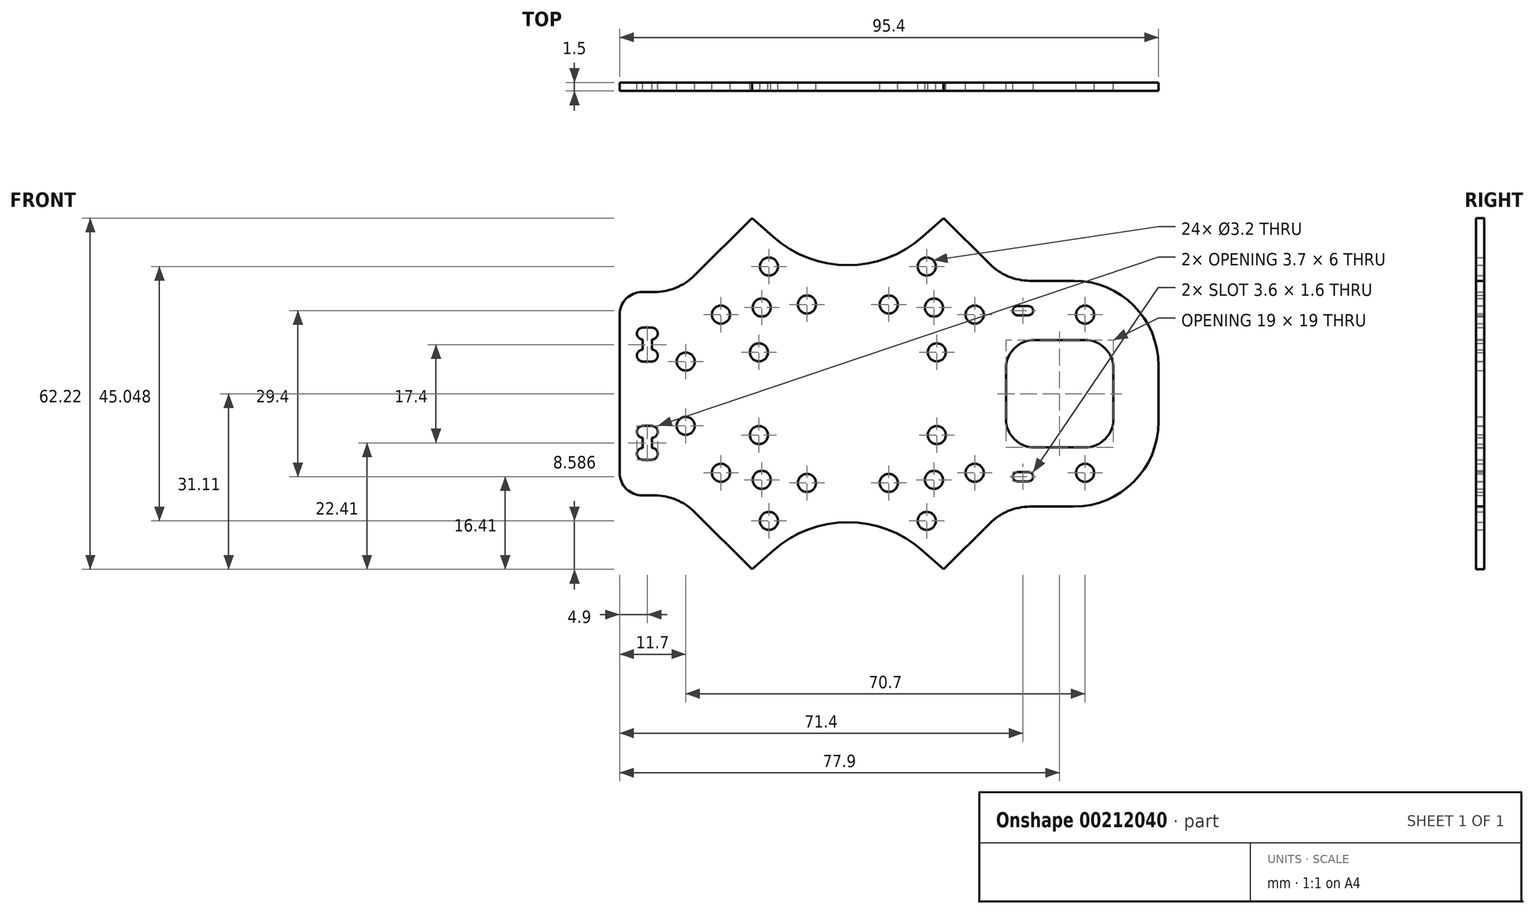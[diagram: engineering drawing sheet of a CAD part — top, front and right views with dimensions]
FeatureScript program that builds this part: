
annotation { "Feature Type Name" : "Feature", "Feature Type Description" : "" }
export const myFeature = defineFeature(function(context is Context, id is Id, definition is map)
    precondition{}
    {
        {
            var Q0;
            Q0=qCreatedBy(makeId("Front.planeOp"),FACE);
            var sketch = newSketch(context, id + "F0", { "sketchPlane" : qUnion([Q0])});
            skPoint(sketch, "E0", {"position": v(0, 0) * mm});
            skCircle(sketch, "E1", {"center": v(15.73, 7.32) * mm, "radius": 1.6 * mm});
            skCircle(sketch, "E2", {"center": v(13.97, 22.52) * mm, "radius": 1.6 * mm});
            skCircle(sketch, "E3", {"center": v(7.25, 15.8) * mm, "radius": 1.6 * mm});
            skCircle(sketch, "E4", {"center": v(22.45, 14) * mm, "radius": 1.6 * mm});
            skCircle(sketch, "E5", {"center": v(15.25, 15.25) * mm, "radius": 1.6 * mm});
            skCircle(sketch, "E6.MirrorC", {"center": v(-15.73, 7.32) * mm, "radius": 1.6 * mm});
            skCircle(sketch, "E7.MirrorC", {"center": v(-13.97, 22.52) * mm, "radius": 1.6 * mm});
            skCircle(sketch, "E8.MirrorC", {"center": v(-7.25, 15.8) * mm, "radius": 1.6 * mm});
            skCircle(sketch, "E9.MirrorC", {"center": v(-22.45, 14) * mm, "radius": 1.6 * mm});
            skCircle(sketch, "E10.MirrorC", {"center": v(-15.25, 15.25) * mm, "radius": 1.6 * mm});
            skCircle(sketch, "E11.MirrorC", {"center": v(-15.25, -15.25) * mm, "radius": 1.6 * mm});
            skCircle(sketch, "E12.MirrorC", {"center": v(-22.45, -14) * mm, "radius": 1.6 * mm});
            skCircle(sketch, "E13.MirrorC", {"center": v(-7.25, -15.8) * mm, "radius": 1.6 * mm});
            skCircle(sketch, "E14.MirrorC", {"center": v(15.73, -7.32) * mm, "radius": 1.6 * mm});
            skCircle(sketch, "E15.MirrorC", {"center": v(-13.97, -22.52) * mm, "radius": 1.6 * mm});
            skCircle(sketch, "E16.MirrorC", {"center": v(-15.73, -7.32) * mm, "radius": 1.6 * mm});
            skCircle(sketch, "E17.MirrorC", {"center": v(15.25, -15.25) * mm, "radius": 1.6 * mm});
            skCircle(sketch, "E18.MirrorC", {"center": v(22.45, -14) * mm, "radius": 1.6 * mm});
            skCircle(sketch, "E19.MirrorC", {"center": v(7.25, -15.8) * mm, "radius": 1.6 * mm});
            skCircle(sketch, "E20.MirrorC", {"center": v(13.97, -22.52) * mm, "radius": 1.6 * mm});
            skLineSegment(sketch, "E21", {"start": v(-25.7, -25.7) * mm, "end": v(60.72, 60.72) * mm, "construction": true});
            skLineSegment(sketch, "E22", {"start": v(16.97, 31.11) * mm, "end": v(25.15, 22.93) * mm});
            skLineSegment(sketch, "E23", {"start": v(16.97, 31.11) * mm, "end": v(13.3, 27.84) * mm});
            skLineSegment(sketch, "E24", {"start": v(0, -54.73) * mm, "end": v(0, 66.02) * mm, "construction": true});
            skLineSegment(sketch, "E25.MirrorCS", {"start": v(-16.97, 31.11) * mm, "end": v(-13.3, 27.84) * mm});
            skLineSegment(sketch, "E26.MirrorCS", {"start": v(-16.97, 31.11) * mm, "end": v(-27.15, 20.93) * mm});
            skPoint(sketch, "E27.visualSharp", {"position": v(0, 16) * mm});
            skArc(sketch, "E27.filletArc", {"start": v(-13.3, 27.84) * mm, "mid": v(0, 22.78) * mm, "end": v(13.3, 27.84) * mm});
            skLineSegment(sketch, "E28.bottom", {"start": v(-34.7, 5.7) * mm, "end": v(-36.3, 5.7) * mm});
            skLineSegment(sketch, "E28.top", {"start": v(-34.7, 11.7) * mm, "end": v(-36.3, 11.7) * mm});
            skLineSegment(sketch, "E28.right", {"start": v(-36.3, 7.8) * mm, "end": v(-36.3, 9.6) * mm});
            skArc(sketch, "E29", {"start": v(-36.3, 11.7) * mm, "mid": v(-37.35, 10.65) * mm, "end": v(-36.3, 9.6) * mm});
            skArc(sketch, "E30", {"start": v(-34.7, 9.6) * mm, "mid": v(-33.65, 10.65) * mm, "end": v(-34.7, 11.7) * mm});
            skArc(sketch, "E31", {"start": v(-36.3, 7.8) * mm, "mid": v(-37.35, 6.75) * mm, "end": v(-36.3, 5.7) * mm});
            skArc(sketch, "E32", {"start": v(-34.7, 5.7) * mm, "mid": v(-33.65, 6.75) * mm, "end": v(-34.7, 7.8) * mm});
            skLineSegment(sketch, "E33.trimOffspring", {"start": v(-34.7, 7.8) * mm, "end": v(-34.7, 9.6) * mm});
            skLineSegment(sketch, "E34.MirrorCS", {"start": v(-34.7, -11.7) * mm, "end": v(-36.3, -11.7) * mm});
            skLineSegment(sketch, "E35.MirrorCS", {"start": v(-34.7, -5.7) * mm, "end": v(-36.3, -5.7) * mm});
            skLineSegment(sketch, "E36.MirrorCS", {"start": v(-36.3, -7.8) * mm, "end": v(-36.3, -9.6) * mm});
            skLineSegment(sketch, "E37.MirrorCS", {"start": v(-34.7, -7.8) * mm, "end": v(-34.7, -9.6) * mm});
            skArc(sketch, "E38.MirrorCS", {"start": v(-36.3, -7.8) * mm, "mid": v(-37.35, -6.75) * mm, "end": v(-36.3, -5.7) * mm});
            skArc(sketch, "E39.MirrorCS", {"start": v(-34.7, -5.7) * mm, "mid": v(-33.65, -6.75) * mm, "end": v(-34.7, -7.8) * mm});
            skArc(sketch, "E40.MirrorCS", {"start": v(-34.7, -9.6) * mm, "mid": v(-33.65, -10.65) * mm, "end": v(-34.7, -11.7) * mm});
            skArc(sketch, "E41.MirrorCS", {"start": v(-36.3, -11.7) * mm, "mid": v(-37.35, -10.65) * mm, "end": v(-36.3, -9.6) * mm});
            skLineSegment(sketch, "E42", {"start": v(87.03, 0) * mm, "end": v(-68.93, 0) * mm, "construction": true});
            skLineSegment(sketch, "E43", {"start": v(-40.4, 0) * mm, "end": v(-40.4, 14) * mm});
            skLineSegment(sketch, "E44", {"start": v(-34.23, 18) * mm, "end": v(-36.4, 18) * mm});
            skPoint(sketch, "E45.visualSharp", {"position": v(-30.08, 18) * mm});
            skArc(sketch, "E45.filletArc", {"start": v(-34.23, 18) * mm, "mid": v(-30.4, 18.76) * mm, "end": v(-27.15, 20.93) * mm});
            skPoint(sketch, "E46.visualSharp", {"position": v(-40.4, 18) * mm});
            skArc(sketch, "E46.filletArc", {"start": v(-36.4, 18) * mm, "mid": v(-39.23, 16.83) * mm, "end": v(-40.4, 14) * mm});
            skLineSegment(sketch, "E47", {"start": v(55, 5) * mm, "end": v(55, 0) * mm});
            skLineSegment(sketch, "E48.MirrorCS", {"start": v(16.97, -31.11) * mm, "end": v(25.15, -22.93) * mm});
            skLineSegment(sketch, "E49.MirrorCS", {"start": v(16.97, -31.11) * mm, "end": v(13.3, -27.84) * mm});
            skArc(sketch, "E50.MirrorCS", {"start": v(-13.3, -27.84) * mm, "mid": v(0, -22.78) * mm, "end": v(13.3, -27.84) * mm});
            skLineSegment(sketch, "E51.MirrorCS", {"start": v(-16.97, -31.11) * mm, "end": v(-13.3, -27.84) * mm});
            skLineSegment(sketch, "E52.MirrorCS", {"start": v(-16.97, -31.11) * mm, "end": v(-27.15, -20.93) * mm});
            skArc(sketch, "E53.MirrorCS", {"start": v(-34.23, -18) * mm, "mid": v(-30.4, -18.76) * mm, "end": v(-27.15, -20.93) * mm});
            skLineSegment(sketch, "E54.MirrorCS", {"start": v(-40.4, 0) * mm, "end": v(-40.4, -14) * mm});
            skLineSegment(sketch, "E55.MirrorCS", {"start": v(-34.23, -18) * mm, "end": v(-36.4, -18) * mm});
            skArc(sketch, "E56.MirrorCS", {"start": v(-36.4, -18) * mm, "mid": v(-39.23, -16.83) * mm, "end": v(-40.4, -14) * mm});
            skCircle(sketch, "E57", {"center": v(42, 14) * mm, "radius": 1.6 * mm});
            skLineSegment(sketch, "E58", {"start": v(40, 20) * mm, "end": v(32.23, 20) * mm});
            skArc(sketch, "E59.filletArc", {"start": v(25.15, 22.93) * mm, "mid": v(28.4, 20.76) * mm, "end": v(32.23, 20) * mm});
            skPoint(sketch, "E60.visualSharp", {"position": v(55, 20) * mm});
            skArc(sketch, "E60.filletArc", {"start": v(55, 5) * mm, "mid": v(50.6, 15.6) * mm, "end": v(40, 20) * mm});
            skCircle(sketch, "E61.MirrorC", {"center": v(42, -14) * mm, "radius": 1.6 * mm});
            skLineSegment(sketch, "E62.MirrorCS", {"start": v(40, -20) * mm, "end": v(32.23, -20) * mm});
            skLineSegment(sketch, "E63.MirrorCS", {"start": v(55, -5) * mm, "end": v(55, 0) * mm});
            skArc(sketch, "E64.MirrorCS", {"start": v(55, -5) * mm, "mid": v(50.6, -15.6) * mm, "end": v(40, -20) * mm});
            skArc(sketch, "E65.MirrorCS", {"start": v(25.15, -22.93) * mm, "mid": v(28.4, -20.76) * mm, "end": v(32.23, -20) * mm});
            skLineSegment(sketch, "E66", {"start": v(28, 0) * mm, "end": v(28, 4.5) * mm});
            skLineSegment(sketch, "E67", {"start": v(33, 9.5) * mm, "end": v(42, 9.5) * mm});
            skLineSegment(sketch, "E68", {"start": v(47, 4.5) * mm, "end": v(47, 0) * mm});
            skPoint(sketch, "E69.visualSharp", {"position": v(28, 9.5) * mm});
            skArc(sketch, "E69.filletArc", {"start": v(33, 9.5) * mm, "mid": v(29.46, 8.04) * mm, "end": v(28, 4.5) * mm});
            skPoint(sketch, "E70.visualSharp", {"position": v(47, 9.5) * mm});
            skArc(sketch, "E70.filletArc", {"start": v(47, 4.5) * mm, "mid": v(45.54, 8.04) * mm, "end": v(42, 9.5) * mm});
            skLineSegment(sketch, "E71.MirrorCS", {"start": v(47, -4.5) * mm, "end": v(47, 0) * mm});
            skArc(sketch, "E72.MirrorCS", {"start": v(47, -4.5) * mm, "mid": v(45.54, -8.04) * mm, "end": v(42, -9.5) * mm});
            skLineSegment(sketch, "E73.MirrorCS", {"start": v(28, 0) * mm, "end": v(28, -4.5) * mm});
            skLineSegment(sketch, "E74.MirrorCS", {"start": v(33, -9.5) * mm, "end": v(42, -9.5) * mm});
            skArc(sketch, "E75.MirrorCS", {"start": v(33, -9.5) * mm, "mid": v(29.46, -8.04) * mm, "end": v(28, -4.5) * mm});
            skCircle(sketch, "E76", {"center": v(-28.7, 5.7) * mm, "radius": 1.6 * mm});
            skCircle(sketch, "E77.MirrorC", {"center": v(-28.7, -5.7) * mm, "radius": 1.6 * mm});
            skLineSegment(sketch, "E78.bottom", {"start": v(30, 15.5) * mm, "end": v(32, 15.5) * mm});
            skLineSegment(sketch, "E78.top", {"start": v(30, 13.9) * mm, "end": v(32, 13.9) * mm});
            skArc(sketch, "E79", {"start": v(32, 13.9) * mm, "mid": v(32.8, 14.7) * mm, "end": v(32, 15.5) * mm});
            skArc(sketch, "E80", {"start": v(30, 15.5) * mm, "mid": v(29.2, 14.7) * mm, "end": v(30, 13.9) * mm});
            skPoint(sketch, "E81.orphan", {"position": v(32, 15.9) * mm});
            skPoint(sketch, "E82.left.end.orphan", {"position": v(30, 13.9) * mm});
            skPoint(sketch, "E83.MirrorP", {"position": v(30, -13.9) * mm});
            skArc(sketch, "E84.MirrorCS", {"start": v(32, -13.9) * mm, "mid": v(32.8, -14.7) * mm, "end": v(32, -15.5) * mm});
            skPoint(sketch, "E85.MirrorP", {"position": v(32, -15.9) * mm});
            skArc(sketch, "E86.MirrorCS", {"start": v(30, -15.5) * mm, "mid": v(29.2, -14.7) * mm, "end": v(30, -13.9) * mm});
            skLineSegment(sketch, "E87.MirrorCS", {"start": v(30, -13.9) * mm, "end": v(32, -13.9) * mm});
            skLineSegment(sketch, "E88.MirrorCS", {"start": v(30, -15.5) * mm, "end": v(32, -15.5) * mm});
            skSolve(sketch);
        }
        {
            var Q0;
            Q0 = qSketchRegion(id + "F0", true);
            extrude(context, id + "F1", {"entities" : qUnion([Q0]), "depth" : 1.5 * mm});
        }
    });
